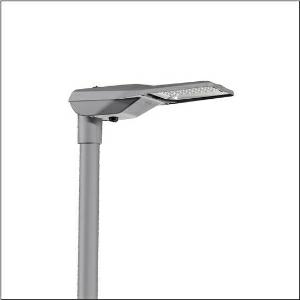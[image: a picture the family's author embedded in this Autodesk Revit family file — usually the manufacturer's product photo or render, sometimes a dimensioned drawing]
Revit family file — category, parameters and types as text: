
# Revit family: streetlight_sl_21_iq_mini___p1_0a_5xe2a31y08gb_f1ed
name_source: partatom
category: Lighting Fixtures
units: mm (PartAtom-declared; Revit-internal decimal feet)

## family parameters
Cut with Voids When Loaded = No
Host = Face
Light Source = No
Part Type = Normal
Room Calculation Point = No
Round Connector Dimension = Use Diameter
Shared = No

## types (1)
- --- (1 x LED, 5990 lm, 39.8 W, 3000K)
    Apparent Load = 40 VA
    CIE Flux Codes = 21 50 90 100 100
    Color Rendering = 70
    Color Temperature = 3000K
    Default Elevation = 1800 mm
    Description = Streetlight SL 21 iQ mini, mast luminaire, primary light control with lens, of PMMA, primary optical cover: cover, of toughened safety glass, transparent, light distribution: P1.0a, light emission: direct distribution, primary light characteristic: asymmetric, installation type: post-top, side-entry, LED, High Power LED, rated luminous flux: 5.990lm, luminous efficacy: 151lm/W, light colour: 730, colour temperature: 3000K, control gear: iQ-Street Remote, D4i with power reduction, control: pre-setting: logarithmic dimming characteristic, Street-Remote, Auto-Match, Temp-Guard, Lumen-Switch, Night-Set, Smart-Wire, Light-Fading, Desk-Remote (wireless, voltage-free reading and setting of iQ features in the workshop via application-optimized NFC function/RFID function), optimised constant luminous flux control (CLO 2.0), mains connection: 220..240V, AC, 50/60Hz, start of lifetime: 40W, end of service life: 41W, reduction: 18W, luminaire housing, of diecast aluminium, powder-coated, SITECO metallic grey (DB 702S), corrosivity category C5 high according to DIN EN ISO 12944, please order mast flange separately, inclination adjustable: 0°, 5°, 10°, 15°, sealing non-destructively replaceable, multi-level sealing system, length: 628mm, width: 235mm, height: 110mm, mast flange for spigot size: 42mm (side-entry): 5XC10008XM4, 60/48mm (side-entry/post-top): 5XC10108XM2, 76/60mm (side-entry/post-top): 5XC10108XM1, mounting height: 4..8m, Smart Interface below and above, protection rating (complete): IP66, insulation class (complete): insulation class II (safety insulation), certification: CE, ENEC, ENEC+, VDE, impact resistance: IK10, permissible operating ambient temperature for outdoor applications: -40..+50°C, standard-compliant lighting for roads and squares, packaging unit: 1 piece

Light Distribution: P1.0a
    Height = 110 mm
    Lamp = 1 x LED
    Lamp Light Flux = 5990 lm
    Lamp Power = 39.8 W
    Lamp count = 1
    Length = 625 mm
    Luminous efficacy = 151 lm/W
    Manufacturer = Siteco
    ModVariant = No
    Model = 5XE2A31Y08GB
    Number of Poles = 1
    OnlyDefault = Yes
    Power Factor = 1
    Product Name = Streetlight SL 21 iQ mini | P1.0a
    Product group = mast luminaire | pylon top
    ProductGroupID = 6100
    Protection Class = Protection class II
    Protection Degree = IP 66
    RLX_Detail_Level = 1
    RLX_Emergency_Light_Flux = 0 lm
    RLX_Emergency_Type = 0
    RLX_Emergency_Type_DB = No
    RlxData = <blob elided: 104093 chars, md5=7640ade1>
    Socket = socket
    Standby Power = 0 W
    System Light Flux = 5990 lm
    System Power = 40 W
    Type Comments = factory setting: luminous flux: 100 % | dim-lin: 254 | 800 mA
    Type Image = l_1003514.jpg
    URL = http://relux.com
    VarID = @adj_113661
    Voltage = 0 V
    Weight = 0.00 kg
    Width = 234 mm

## geometry (parser evidence)
native form markers: Blend x4, Sweep x11
no freeform markers — native parametric forms only
